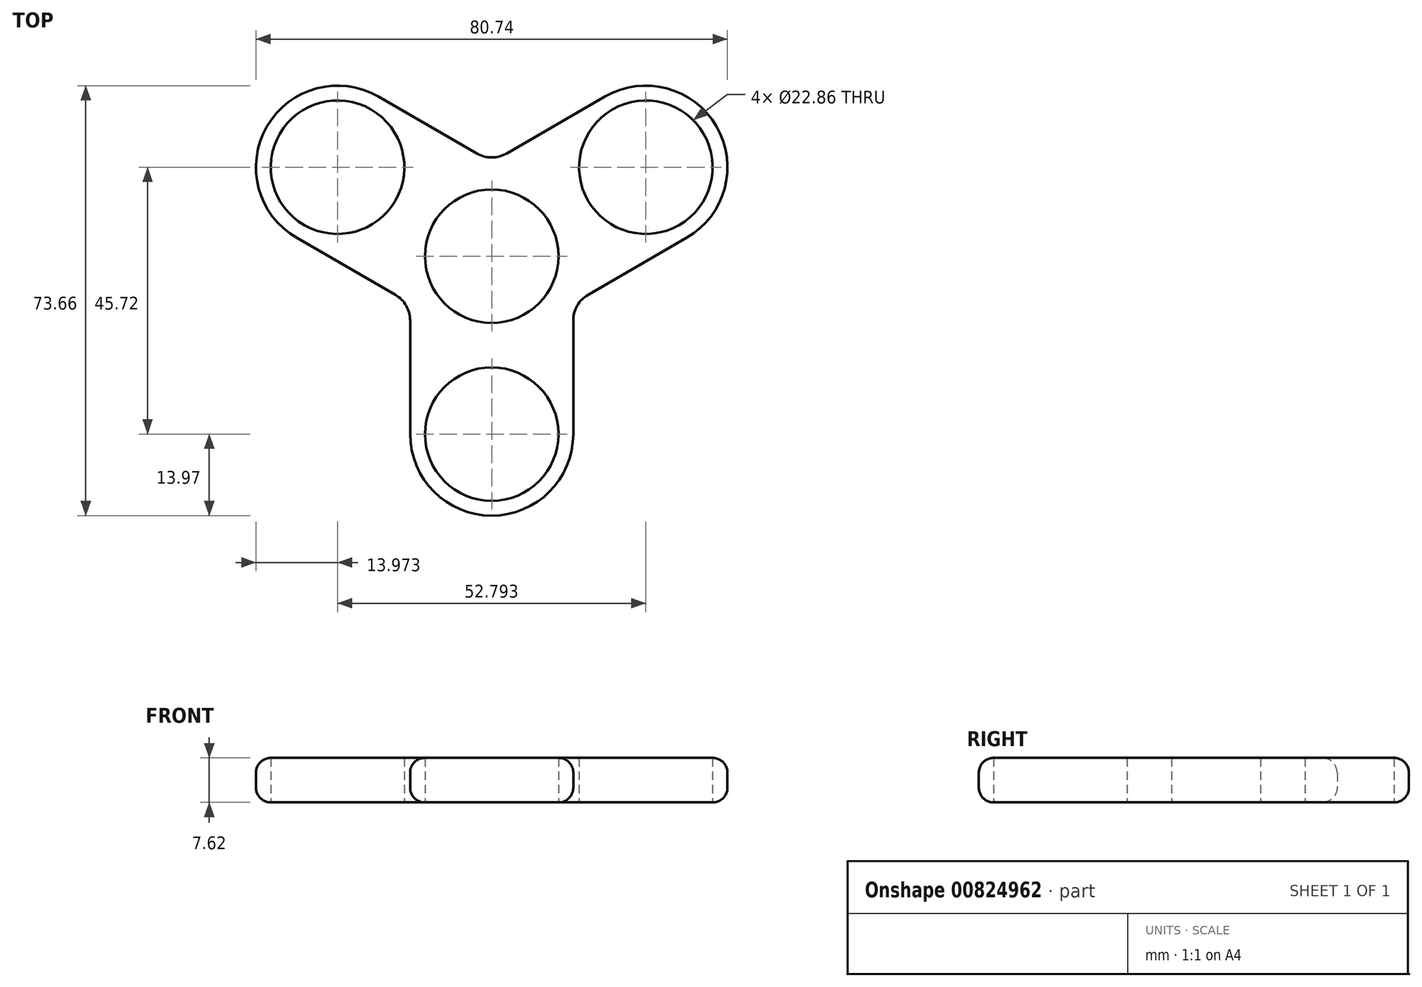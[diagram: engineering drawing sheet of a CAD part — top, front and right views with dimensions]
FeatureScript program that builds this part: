
annotation { "Feature Type Name" : "Feature", "Feature Type Description" : "" }
export const myFeature = defineFeature(function(context is Context, id is Id, definition is map)
    precondition{}
    {
        {
            var Q0;
            Q0=qCreatedBy(makeId("Top.planeOp"),FACE);
            var sketch = newSketch(context, id + "F0", { "sketchPlane" : qUnion([Q0])});
            skCircle(sketch, "E0", {"center": v(0, 0) * mm, "radius": 13.97 * mm});
            skCircle(sketch, "E1", {"center": v(-26.4, 15.24) * mm, "radius": 11.43 * mm});
            skCircle(sketch, "E2", {"center": v(0, 0) * mm, "radius": 11.43 * mm});
            skCircle(sketch, "E3", {"center": v(-26.4, 15.24) * mm, "radius": 13.97 * mm});
            skLineSegment(sketch, "E4", {"start": v(0, 0) * mm, "end": v(-26.4, 15.24) * mm});
            skCircle(sketch, "E5.1.0", {"center": v(0, -30.48) * mm, "radius": 13.97 * mm});
            skCircle(sketch, "E5.2.0", {"center": v(26.4, 15.24) * mm, "radius": 13.97 * mm});
            skCircle(sketch, "E6.1.0", {"center": v(0, -30.48) * mm, "radius": 11.43 * mm});
            skLineSegment(sketch, "E6.1.1", {"start": v(0, 0) * mm, "end": v(0, -30.48) * mm});
            skCircle(sketch, "E6.2.0", {"center": v(26.4, 15.24) * mm, "radius": 11.43 * mm});
            skLineSegment(sketch, "E6.2.1", {"start": v(0, 0) * mm, "end": v(26.4, 15.24) * mm});
            skLineSegment(sketch, "E7.bottom", {"start": v(13.97, 0) * mm, "end": v(-13.97, 0) * mm});
            skLineSegment(sketch, "E7.top", {"start": v(13.97, -30.48) * mm, "end": v(-13.97, -30.48) * mm});
            skLineSegment(sketch, "E7.left", {"start": v(13.97, 0) * mm, "end": v(13.97, -30.48) * mm});
            skLineSegment(sketch, "E7.right", {"start": v(-13.97, 0) * mm, "end": v(-13.97, -30.48) * mm});
            skPoint(sketch, "E7.middle", {"position": v(0, -15.24) * mm});
            skLineSegment(sketch, "E8.1.0", {"start": v(19.41, 27.34) * mm, "end": v(33.38, 3.14) * mm});
            skLineSegment(sketch, "E8.1.1", {"start": v(6.98, -12.1) * mm, "end": v(33.38, 3.14) * mm});
            skLineSegment(sketch, "E8.1.2", {"start": v(-6.99, 12.1) * mm, "end": v(19.41, 27.34) * mm});
            skLineSegment(sketch, "E8.1.3", {"start": v(-6.99, 12.1) * mm, "end": v(6.99, -12.1) * mm});
            skLineSegment(sketch, "E8.2.0", {"start": v(-33.38, 3.14) * mm, "end": v(-19.41, 27.34) * mm});
            skLineSegment(sketch, "E8.2.1", {"start": v(6.99, 12.1) * mm, "end": v(-19.41, 27.34) * mm});
            skLineSegment(sketch, "E8.2.2", {"start": v(-6.99, -12.1) * mm, "end": v(-33.38, 3.14) * mm});
            skLineSegment(sketch, "E8.2.3", {"start": v(-6.99, -12.1) * mm, "end": v(6.99, 12.1) * mm});
            skSolve(sketch);
        }
        {
            var Q0;
            Q0=qSketchRegion(id+"F0",true);
            var Q1;
            {var subQ1=sQuery(id+"F0.wireOp",EDGE,"E0");var subQ7=makeQuery(id+"F0.imprint","INTERSECT",VERTEX,{"derivedFrom":[subQ1,sQuery(id+"F0.wireOp",EDGE,"2a81f7ea-dfaa-4220-9730-6b88422f781c.2.0")]});Q1=makeQuery(id+"F0.imprint","IMPRINT",FACE,{"disambiguationData":[TD([[makeQuery(id+"F0.imprint","IMPRINT",EDGE,{"disambiguationData":[TD([[subQ7,-1.0]])],"derivedFrom":subQ1}),1.0]])]});}
            var Q2;
            {var subQ3=sQuery(id+"F0.wireOp",EDGE,"E4");var subQ5=sQuery(id+"F0.wireOp",EDGE,"E2");var subQ6=makeQuery(id+"F0.imprint","INTERSECT",VERTEX,{"derivedFrom":[subQ5,subQ3]});Q2=makeQuery(id+"F0.imprint","IMPRINT",FACE,{"disambiguationData":[TD([[makeQuery(id+"F0.imprint","IMPRINT",EDGE,{"disambiguationData":[TD([[subQ6,-1.0]])],"derivedFrom":subQ5}),-1.0]])]});}
            var Q3;
            {var subQ5=sQuery(id+"F0.wireOp",EDGE,"E0");var subQ8=makeQuery(id+"F0.imprint","INTERSECT",VERTEX,{"derivedFrom":[subQ5,sQuery(id+"F0.wireOp",EDGE,"ad422b94-503c-4b8c-a564-e47813131238.2.1")]});Q3=makeQuery(id+"F0.imprint","IMPRINT",FACE,{"disambiguationData":[TD([[makeQuery(id+"F0.imprint","IMPRINT",EDGE,{"disambiguationData":[TD([[subQ8,1.0]])],"derivedFrom":subQ5}),1.0]])]});}
            var Q4;
            {var subQ3=sQuery(id+"F0.wireOp",EDGE,"KG0W6A2v-qbmV-kile-noT2-Lh5GOKsosSiX");var subQ5=sQuery(id+"F0.wireOp",EDGE,"E2");var subQ6=makeQuery(id+"F0.imprint","INTERSECT",VERTEX,{"derivedFrom":[subQ5,subQ3]});Q4=makeQuery(id+"F0.imprint","IMPRINT",FACE,{"disambiguationData":[TD([[makeQuery(id+"F0.imprint","IMPRINT",EDGE,{"disambiguationData":[TD([[subQ6,1.0]])],"derivedFrom":subQ5}),-1.0]])]});}
            var Q5;
            {var subQ1=sQuery(id+"F0.wireOp",EDGE,"E0");var subQ7=makeQuery(id+"F0.imprint","INTERSECT",VERTEX,{"derivedFrom":[subQ1,sQuery(id+"F0.wireOp",EDGE,"ad422b94-503c-4b8c-a564-e47813131238.1.1")]});Q5=makeQuery(id+"F0.imprint","IMPRINT",FACE,{"disambiguationData":[TD([[makeQuery(id+"F0.imprint","IMPRINT",EDGE,{"disambiguationData":[TD([[subQ7,1.0]])],"derivedFrom":subQ1}),1.0]])]});}
            extrude(context, id + "F1", {"entities" : qUnion([Q0, Q1, Q2, Q3, Q4, Q5]), "depth" : 7.62 * mm, "offsetDistance" : 25.4 * mm});
        }
        {
            var Q0;
            Q0=makeQuery(id+"F1.opExtrude","SWEPT_EDGE",EDGE,{"disambiguationData":[OSD([sQuery(id+"F0.wireOp",EDGE,"E8.1.2"),sQuery(id+"F0.wireOp",EDGE,"E8.2.1")])]});
            var Q1;
            Q1=makeQuery(id+"F1.opExtrude","SWEPT_EDGE",EDGE,{"disambiguationData":[OSD([sQuery(id+"F0.wireOp",EDGE,"E7.left"),sQuery(id+"F0.wireOp",EDGE,"E8.1.1")])]});
            var Q2;
            Q2=makeQuery(id+"F1.opExtrude","SWEPT_EDGE",EDGE,{"disambiguationData":[OSD([sQuery(id+"F0.wireOp",EDGE,"E7.right"),sQuery(id+"F0.wireOp",EDGE,"E8.2.2")])]});
            fillet(context, id + "F2", {"entities" : qUnion([Q0, Q1, Q2]), "radius" : 5.08 * mm, "tangentPropagation" : true, "allowEdgeOverflow" : false});
        }
        {
            var Q0;
            Q0=makeQuery(id+"F1.opExtrude","CAP_EDGE",EDGE,{"disambiguationData":[OSD([sQuery(id+"F0.wireOp",EDGE,"E8.1.1")])],"isStart":false});
            var Q1;
            {var subQ0=sQuery(id+"F0.wireOp",EDGE,"E8.1.1");var subQ1=sQuery(id+"F0.wireOp",EDGE,"E7.left");Q1=makeQuery(id+"F2.opFillet","BLEND_EDGE",EDGE,{"blendedFrom":[makeQuery(id+"F1.opExtrude","SWEPT_EDGE",EDGE,{"disambiguationData":[OSD([subQ1,subQ0])]}),makeQuery(id+"F1.opExtrude","CAP_FACE",FACE,{"disambiguationData":[OSD([sQuery(id+"F0.wireOp",EDGE,"E1"),sQuery(id+"F0.wireOp",EDGE,"E2"),sQuery(id+"F0.wireOp",EDGE,"E3"),sQuery(id+"F0.wireOp",EDGE,"E5.1.0"),sQuery(id+"F0.wireOp",EDGE,"E5.2.0"),sQuery(id+"F0.wireOp",EDGE,"E6.1.0"),sQuery(id+"F0.wireOp",EDGE,"E6.2.0"),subQ1,sQuery(id+"F0.wireOp",EDGE,"E7.right"),subQ0,sQuery(id+"F0.wireOp",EDGE,"E8.1.2"),sQuery(id+"F0.wireOp",EDGE,"E8.2.1"),sQuery(id+"F0.wireOp",EDGE,"E8.2.2")])],"isStart":false})],"blendedInto":[makeQuery(id+"F1.opExtrude","CAP_FACE",FACE,{"disambiguationData":[OSD([sQuery(id+"F0.wireOp",EDGE,"E1"),sQuery(id+"F0.wireOp",EDGE,"E2"),sQuery(id+"F0.wireOp",EDGE,"E3"),sQuery(id+"F0.wireOp",EDGE,"E5.1.0"),sQuery(id+"F0.wireOp",EDGE,"E5.2.0"),sQuery(id+"F0.wireOp",EDGE,"E6.1.0"),sQuery(id+"F0.wireOp",EDGE,"E6.2.0"),subQ1,sQuery(id+"F0.wireOp",EDGE,"E7.right"),subQ0,sQuery(id+"F0.wireOp",EDGE,"E8.1.2"),sQuery(id+"F0.wireOp",EDGE,"E8.2.1"),sQuery(id+"F0.wireOp",EDGE,"E8.2.2")])],"isStart":false})]});}
            var Q2;
            Q2=makeQuery(id+"F1.opExtrude","CAP_EDGE",EDGE,{"disambiguationData":[OSD([sQuery(id+"F0.wireOp",EDGE,"E7.right")])],"isStart":true});
            fillet(context, id + "F3", {"entities" : qUnion([Q0, Q1, Q2]), "radius" : 2.54 * mm, "tangentPropagation" : true, "allowEdgeOverflow" : false});
        }
    });
